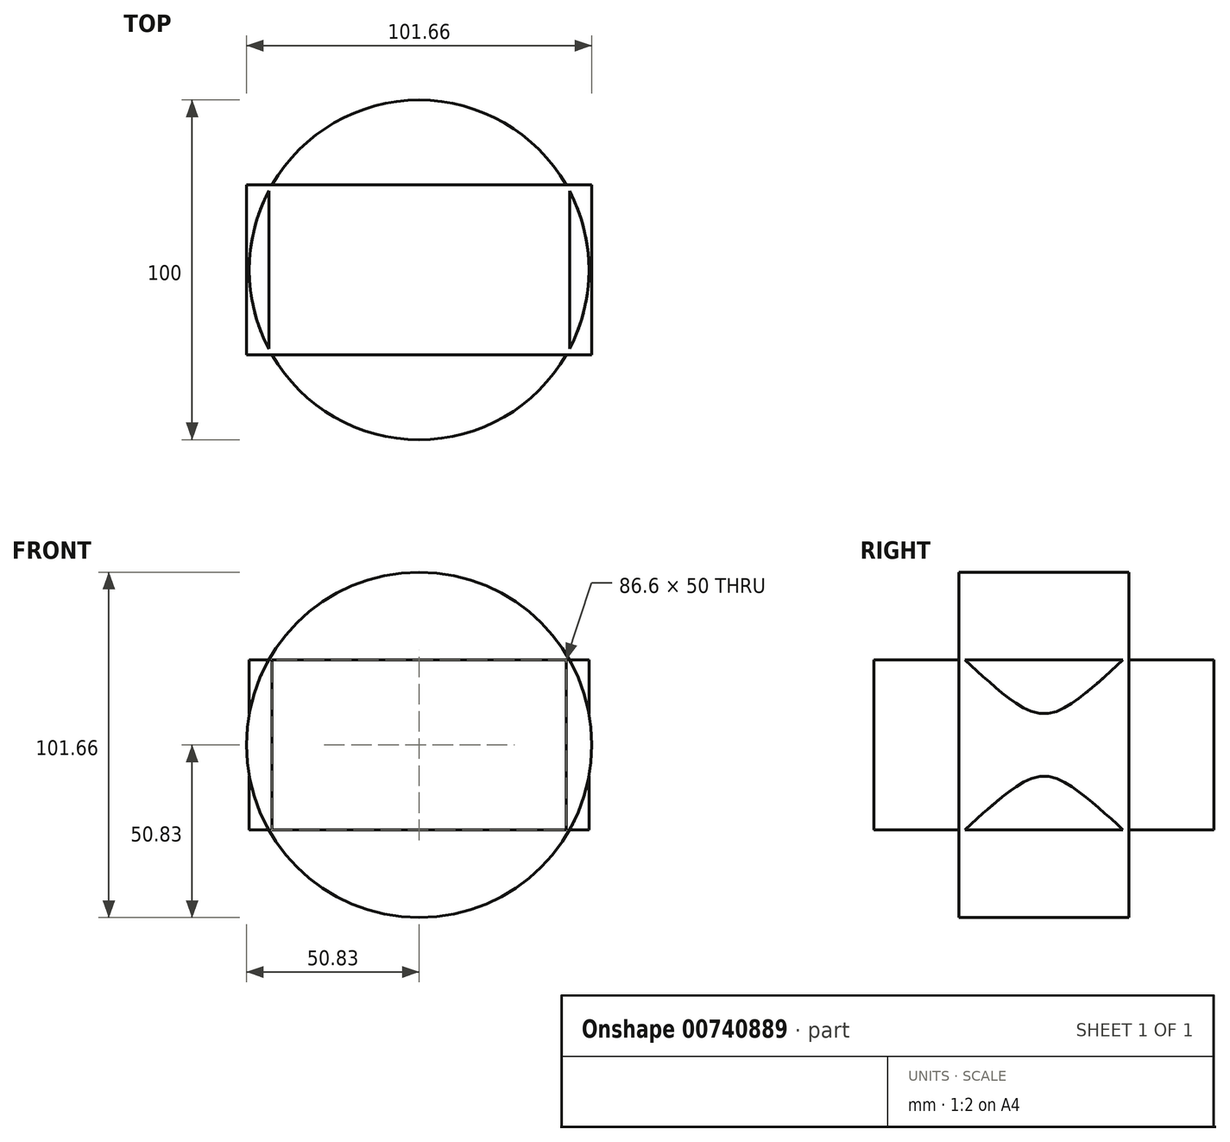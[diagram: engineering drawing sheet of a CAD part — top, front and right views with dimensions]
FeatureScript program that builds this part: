
annotation { "Feature Type Name" : "Feature", "Feature Type Description" : "" }
export const myFeature = defineFeature(function(context is Context, id is Id, definition is map)
    precondition{}
    {
        {
            var Q0;
            Q0=qCreatedBy(makeId("Top.planeOp"),FACE);
            var sketch = newSketch(context, id + "F0", { "sketchPlane" : qUnion([Q0])});
            skCircle(sketch, "E0", {"center": v(0, 0) * mm, "radius": 40 * mm});
            skCircle(sketch, "E1", {"center": v(0, 0) * mm, "radius": 50 * mm});
            skSolve(sketch);
        }
        {
            var Q0;
            Q0 = qSketchRegion(id + "F0", true);
            var sketch = newSketch(context, id + "F1", { "sketchPlane" : qUnion([Q0])});
            skSolve(sketch);
        }
        {
            var Q0;
            Q0=qCreatedBy(makeId("Front.planeOp"),FACE);
            var sketch = newSketch(context, id + "F2", { "sketchPlane" : qUnion([Q0])});
            skCircle(sketch, "E2", {"center": v(0, 0) * mm, "radius": 50.83 * mm});
            skCircle(sketch, "E3", {"center": v(0, 0) * mm, "radius": 3.47 * mm});
            skCircle(sketch, "E4", {"center": v(0, 0) * mm, "radius": 38.6 * mm});
            skSolve(sketch);
        }
        {
            var Q0;
            Q0=makeQuery(id+"F1.imprint","IMPRINT",FACE,{"disambiguationData":[TD([[makeQuery(id+"F1.imprint","IMPRINT",EDGE,{"derivedFrom":makeQuery(id+"F0.imprint","IMPRINT",EDGE,{"derivedFrom":sQuery(id+"F0.wireOp",EDGE,"E0")})}),1.0]])]});
            var Q1;
            Q1=makeQuery(id+"F1.imprint","IMPRINT",FACE,{"disambiguationData":[TD([[makeQuery(id+"F1.imprint","IMPRINT",EDGE,{"derivedFrom":makeQuery(id+"F0.imprint","IMPRINT",EDGE,{"derivedFrom":sQuery(id+"F0.wireOp",EDGE,"E0")})}),-1.0]])]});
            extrude(context, id + "F3", {"entities" : qUnion([Q0, Q1]), "endBound" : BoundingType.SYMMETRIC, "depth" : 50 * mm, "offsetDistance" : 25 * mm});
        }
        {
            var Q0;
            Q0=makeQuery(id+"F2.imprint","IMPRINT",FACE,{"disambiguationData":[TD([[makeQuery(id+"F2.imprint","IMPRINT",EDGE,{"derivedFrom":sQuery(id+"F2.wireOp",EDGE,"E3")}),-1.0]])]});
            var Q1;
            Q1=makeQuery(id+"F2.imprint","IMPRINT",FACE,{"disambiguationData":[TD([[makeQuery(id+"F2.imprint","IMPRINT",EDGE,{"derivedFrom":sQuery(id+"F2.wireOp",EDGE,"E2")}),1.0]])]});
            extrude(context, id + "F4", {"entities" : qUnion([Q0, Q1]), "operationType" : NewBodyOperationType.ADD, "endBound" : BoundingType.SYMMETRIC, "depth" : 50 * mm, "offsetDistance" : 25 * mm});
        }
    });
